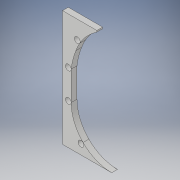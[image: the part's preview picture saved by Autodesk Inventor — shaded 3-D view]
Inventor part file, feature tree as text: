
AUTODESK INVENTOR PART (.ipt)
format: ipt  version: 2018 (Build 220112000, 112)  size: 179,200 bytes
history: native  units: in
note: dims shown in document units (in); Inventor stores cm internally (conversion verified against a paired STEP export)
features: extrude x1, sketch x1
ambient origin geometry x8: Origin, YZ Plane, XZ Plane, XY Plane, X Axis, Y Axis, Z Axis, Center Point
bodies: Body1 (feature_tree)
feature tree (2):
  extrude  "Extrusion3"  Depth=1.0in
  sketch  "Sketch1"  dims[d0=24.0in d1=8.25in d2=12.0in d3=6.5in d4=6.5in d5=12.0in d6=7.0in d7=7.0in d8=1.0in d9=0.5in d10=135.0deg d11=6.5in d12=135.0deg d13=6.5in d14=7.0in d15=0.625in d16=1.0in d17=5.0in d18=0.625in d19=1.0in d20=5.0in d21=3.0in d22=6.0in d23=1.0in d24=2.0in d25=5.0in d26=0.8727in d33=6.25in d34=0.8727in d35=1.0994in d36=6.25in d37=180.0deg d45=150.0deg d46=6.25in d47=180.0deg d48=0.5in d49=0.5in d50=0.5in d52=0.5in d53=1.0in d55=8.4437in d56=0.875in d57=0.875in d58=0.875in d59=0.875in d60=5.3033in d72=25.5in d73=20.0in d74=90.0deg d77=5.9332in d78=0.6126in d79=1.0in d80=0.0in]
